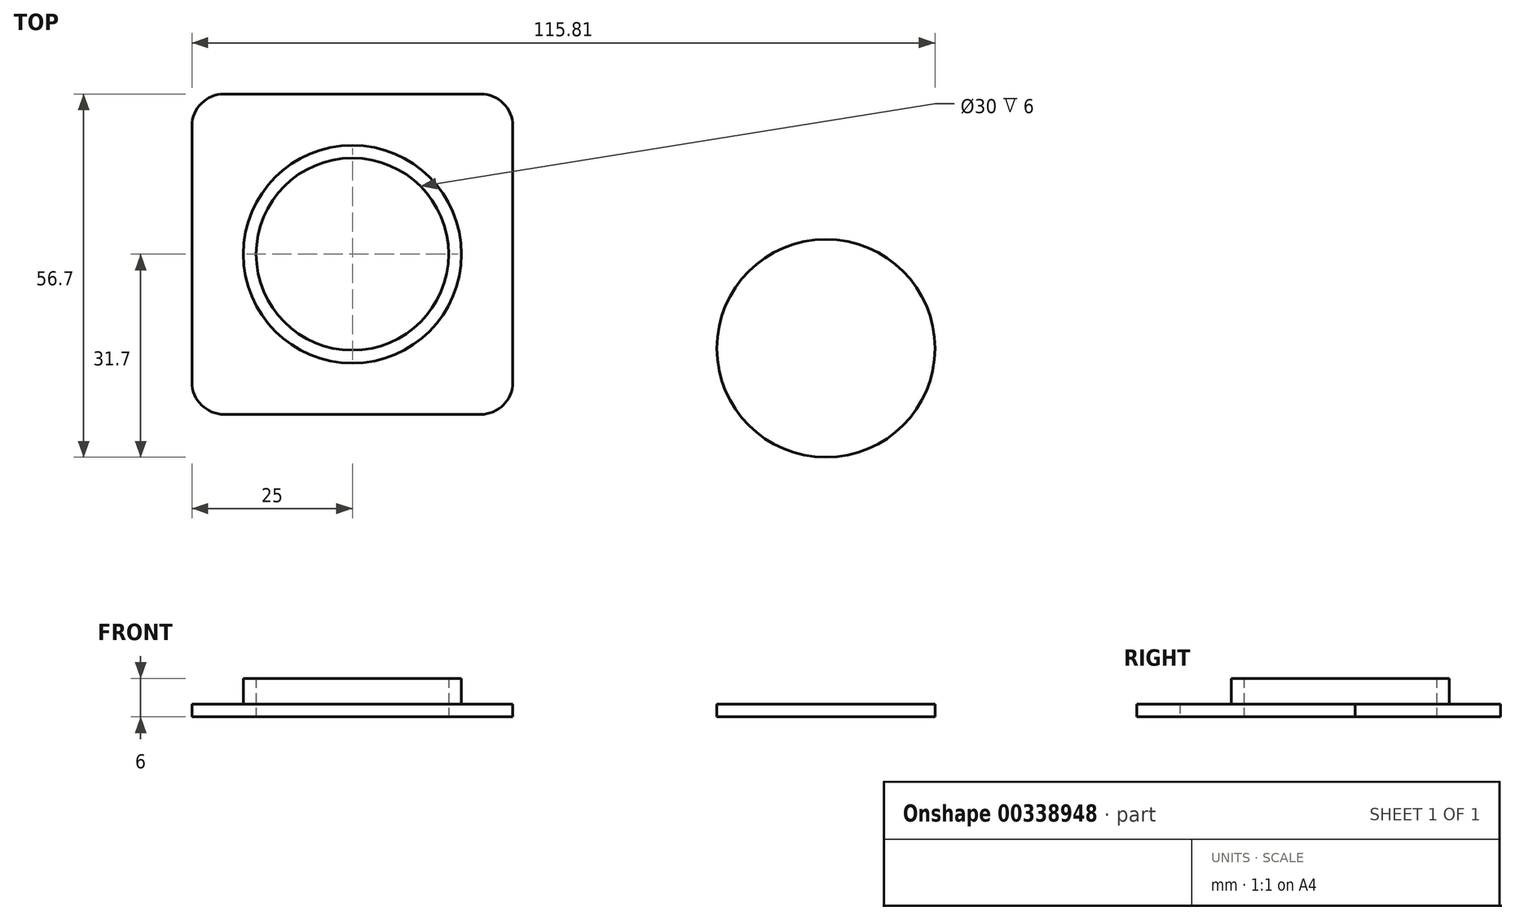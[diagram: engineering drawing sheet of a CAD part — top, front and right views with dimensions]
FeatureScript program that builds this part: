
annotation { "Feature Type Name" : "Feature", "Feature Type Description" : "" }
export const myFeature = defineFeature(function(context is Context, id is Id, definition is map)
    precondition{}
    {
        {
            var Q0;
            Q0=qCreatedBy(makeId("Top.planeOp"),FACE);
            var sketch = newSketch(context, id + "F0", { "sketchPlane" : qUnion([Q0])});
            skLineSegment(sketch, "E0.bottom", {"start": v(-25, 25) * mm, "end": v(25, 25) * mm});
            skLineSegment(sketch, "E0.top", {"start": v(-25, -25) * mm, "end": v(25, -25) * mm});
            skLineSegment(sketch, "E0.left", {"start": v(-25, 25) * mm, "end": v(-25, -25) * mm});
            skLineSegment(sketch, "E0.right", {"start": v(25, 25) * mm, "end": v(25, -25) * mm});
            skCircle(sketch, "E1", {"center": v(0, 0) * mm, "radius": 15 * mm});
            skCircle(sketch, "E2", {"center": v(73.81, -14.7) * mm, "radius": 17 * mm});
            skSolve(sketch);
        }
        {
            var Q0;
            Q0=makeQuery(id+"F0.imprint","IMPRINT",FACE,{"disambiguationData":[TD([[makeQuery(id+"F0.imprint","IMPRINT",EDGE,{"derivedFrom":sQuery(id+"F0.wireOp",EDGE,"E0.bottom")}),-1.0]])]});
            var Q1;
            Q1=makeQuery(id+"F0.imprint","IMPRINT",FACE,{"disambiguationData":[TD([[makeQuery(id+"F0.imprint","IMPRINT",EDGE,{"derivedFrom":sQuery(id+"F0.wireOp",EDGE,"E2")}),1.0]])]});
            extrude(context, id + "F1", {"entities" : qUnion([Q0, Q1]), "depth" : 2 * mm});
        }
        {
            var Q0;
            Q0=makeQuery(id+"F1.opExtrude","SWEPT_EDGE",EDGE,{"disambiguationData":[OSD([sQuery(id+"F0.wireOp",EDGE,"E0.top"),sQuery(id+"F0.wireOp",EDGE,"E0.right")])]});
            var Q1;
            Q1=makeQuery(id+"F1.opExtrude","SWEPT_EDGE",EDGE,{"disambiguationData":[OSD([sQuery(id+"F0.wireOp",EDGE,"E0.bottom"),sQuery(id+"F0.wireOp",EDGE,"E0.right")])]});
            var Q2;
            Q2=makeQuery(id+"F1.opExtrude","SWEPT_EDGE",EDGE,{"disambiguationData":[OSD([sQuery(id+"F0.wireOp",EDGE,"E0.top"),sQuery(id+"F0.wireOp",EDGE,"E0.left")])]});
            var Q3;
            Q3=makeQuery(id+"F1.opExtrude","SWEPT_EDGE",EDGE,{"disambiguationData":[OSD([sQuery(id+"F0.wireOp",EDGE,"E0.bottom"),sQuery(id+"F0.wireOp",EDGE,"E0.left")])]});
            fillet(context, id + "F2", {"entities" : qUnion([Q0, Q1, Q2, Q3]), "radius" : 5 * mm, "tangentPropagation" : true, "allowEdgeOverflow" : false});
        }
        {
            var Q0;
            Q0=makeQuery(id+"F1.opExtrude","CAP_FACE",FACE,{"disambiguationData":[OSD([sQuery(id+"F0.wireOp",EDGE,"E0.bottom"),sQuery(id+"F0.wireOp",EDGE,"E0.top"),sQuery(id+"F0.wireOp",EDGE,"E0.left"),sQuery(id+"F0.wireOp",EDGE,"E0.right"),sQuery(id+"F0.wireOp",EDGE,"E1")])],"isStart":false});
            var sketch = newSketch(context, id + "F3", { "sketchPlane" : qUnion([Q0])});
            skCircle(sketch, "E3", {"center": v(0, 0) * mm, "radius": 17 * mm});
            skSolve(sketch);
        }
        {
            var Q0;
            Q0=makeQuery(id+"F3.imprint","IMPRINT",FACE,{"disambiguationData":[TD([[makeQuery(id+"F3.imprint","IMPRINT",EDGE,{"derivedFrom":sQuery(id+"F3.wireOp",EDGE,"E3")}),1.0]])]});
            extrude(context, id + "F4", {"entities" : qUnion([Q0]), "operationType" : NewBodyOperationType.ADD, "depth" : 4 * mm});
        }
    });
